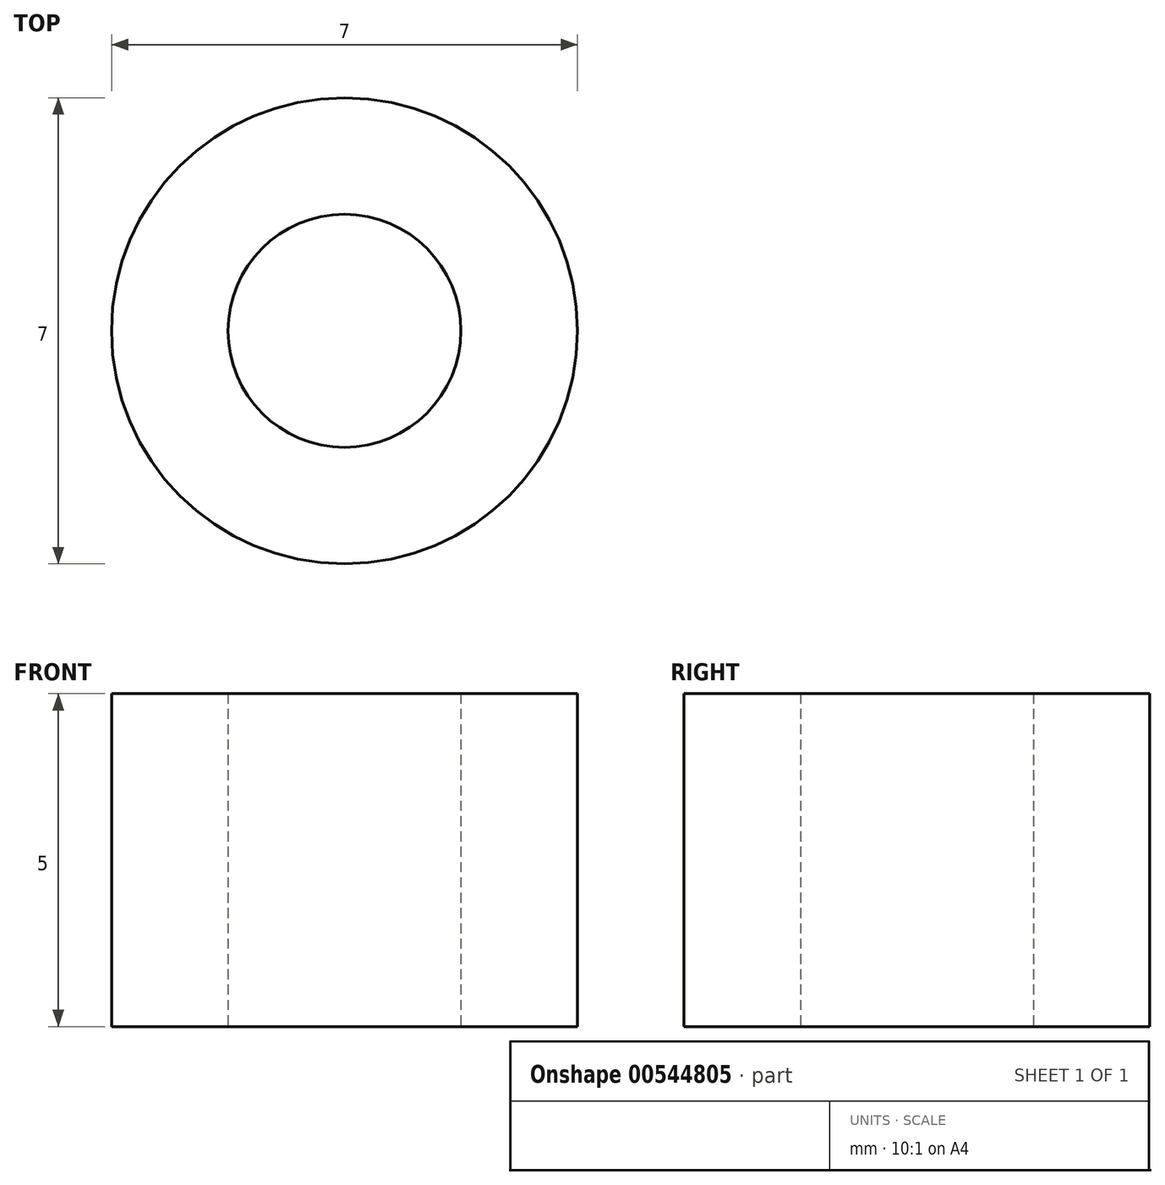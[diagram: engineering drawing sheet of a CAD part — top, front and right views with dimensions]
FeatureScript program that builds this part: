
annotation { "Feature Type Name" : "Feature", "Feature Type Description" : "" }
export const myFeature = defineFeature(function(context is Context, id is Id, definition is map)
    precondition{}
    {
        {
            var Q0;
            Q0=qCreatedBy(makeId("Top.planeOp"),FACE);
            var sketch = newSketch(context, id + "F0", { "sketchPlane" : qUnion([Q0])});
            skCircle(sketch, "E0", {"center": v(0, 0) * mm, "radius": 1.75 * mm});
            skCircle(sketch, "E1", {"center": v(0, 0) * mm, "radius": 3.5 * mm});
            skSolve(sketch);
        }
        {
            var Q0;
            Q0=makeQuery(id+"F0.imprint","IMPRINT",FACE,{"disambiguationData":[TD([[makeQuery(id+"F0.imprint","IMPRINT",EDGE,{"derivedFrom":sQuery(id+"F0.wireOp",EDGE,"E0")}),-1.0]])]});
            extrude(context, id + "F1", {"entities" : qUnion([Q0]), "depth" : 5 * mm, "offsetDistance" : 25 * mm});
        }
    });
